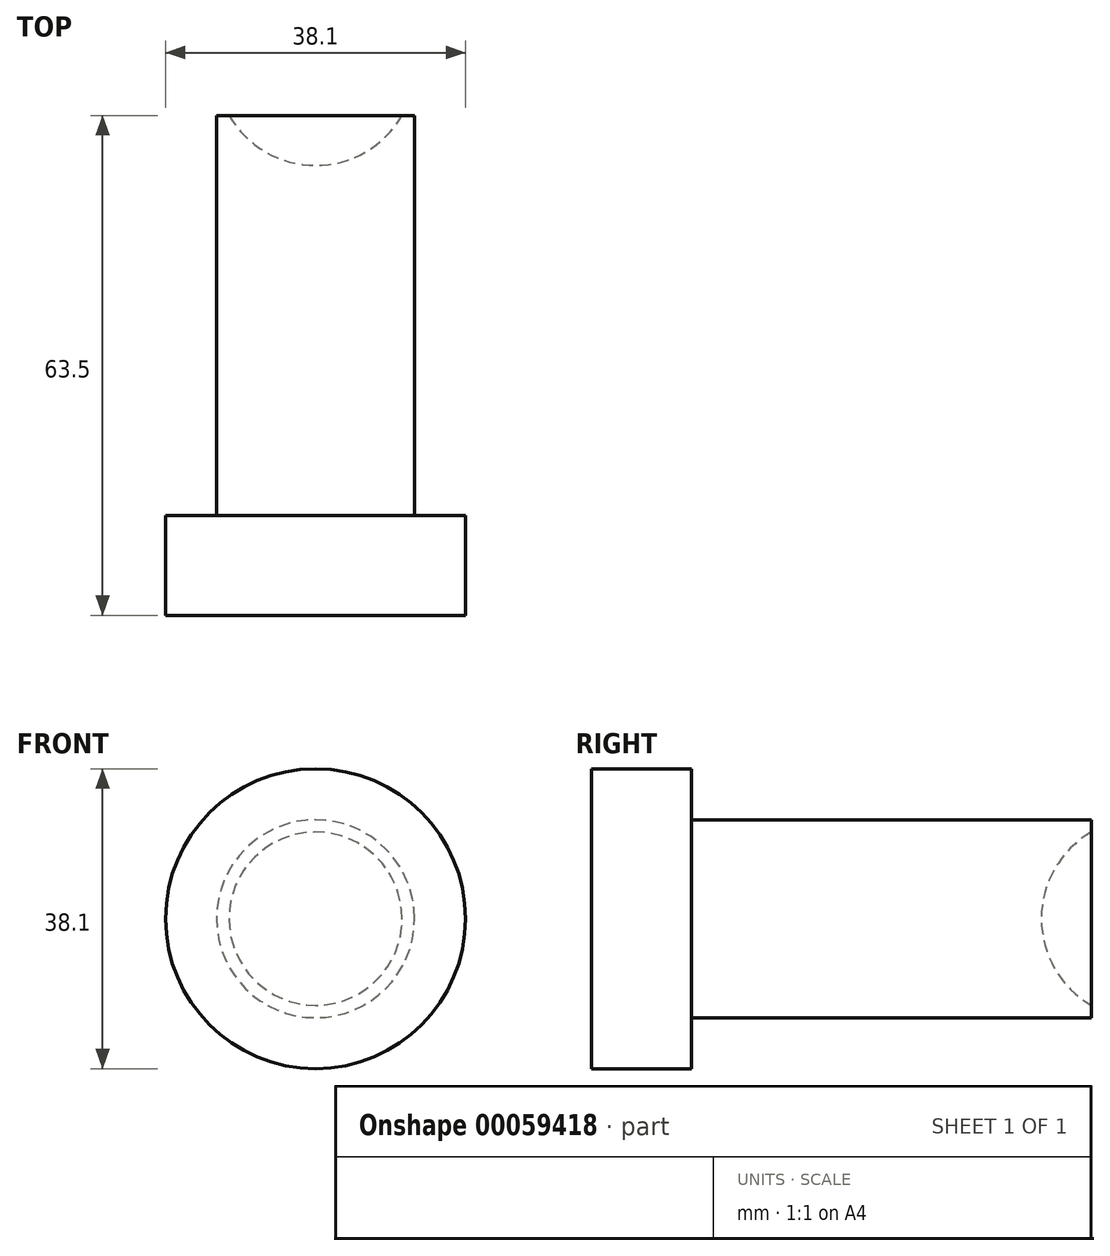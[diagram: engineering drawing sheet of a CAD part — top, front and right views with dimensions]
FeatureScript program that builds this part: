
annotation { "Feature Type Name" : "Feature", "Feature Type Description" : "" }
export const myFeature = defineFeature(function(context is Context, id is Id, definition is map)
    precondition{}
    {
        {
            var Q0;
            Q0=qCreatedBy(makeId("Front.planeOp"),FACE);
            var sketch = newSketch(context, id + "F0", { "sketchPlane" : qUnion([Q0])});
            skCircle(sketch, "E0", {"center": v(0, 0) * mm, "radius": 19.05 * mm});
            skSolve(sketch);
        }
        {
            var Q0;
            Q0 = qSketchRegion(id + "F0", true);
            var Q1;
            Q1=makeQuery(id+"F0.imprint","IMPRINT",FACE,{"disambiguationData":[TD([[makeQuery(id+"F0.imprint","IMPRINT",EDGE,{"derivedFrom":sQuery(id+"F0.wireOp",EDGE,"E0")}),1.0]])]});
            extrude(context, id + "F1", {"entities" : qUnion([Q0, Q1]), "depth" : 12.7 * mm});
        }
        {
            var Q0;
            Q0=qCreatedBy(makeId("Front.planeOp"),FACE);
            var sketch = newSketch(context, id + "F2", { "sketchPlane" : qUnion([Q0])});
            skCircle(sketch, "E1", {"center": v(0, 0) * mm, "radius": 12.57 * mm});
            skSolve(sketch);
        }
        {
            var Q0;
            Q0 = qSketchRegion(id + "F2", true);
            extrude(context, id + "F3", {"entities" : qUnion([Q0]), "operationType" : NewBodyOperationType.ADD, "oppositeDirection" : true, "depth" : 50.8 * mm});
        }
        {
            var Q0;
            Q0=qCreatedBy(makeId("Front.planeOp"),FACE);
            cPlane(context, id + "F4", {"entities" : qUnion([Q0]), "cplaneType" : CPlaneType.OFFSET, "offset" : 57.15 * mm, "oppositeDirection" : true, "width" : 152.4 * mm, "height" : 152.4 * mm});
        }
        {
            var Q0;
            Q0=qCreatedBy(id+"F4.planeOp",FACE);
            var sketch = newSketch(context, id + "F5", { "sketchPlane" : qUnion([Q0])});
            skArc(sketch, "E2", {"start": v(0, 12.7) * mm, "mid": v(-12.7, 0) * mm, "end": v(0, -12.7) * mm});
            skLineSegment(sketch, "E3", {"start": v(0, 12.7) * mm, "end": v(0, -12.7) * mm});
            skSolve(sketch);
        }
        {
            var Q0;
            Q0 = qSketchRegion(id + "F5", true);
            var Q1;
            Q1=sQuery(id+"F5.wireOp",EDGE,"E3");
            revolve(context, id + "F6", {"operationType" : NewBodyOperationType.REMOVE, "entities" : qUnion([Q0]), "axis" : qUnion([Q1]), "revolveType" : RevolveType.FULL, "oppositeDirection" : true});
        }
    });
